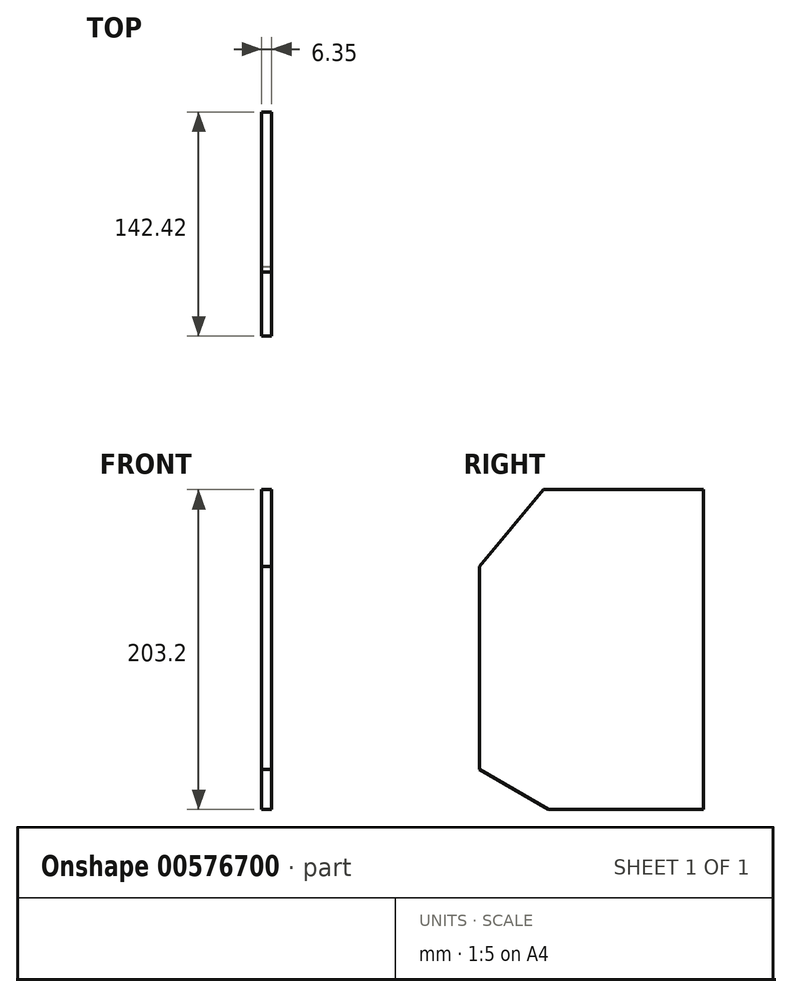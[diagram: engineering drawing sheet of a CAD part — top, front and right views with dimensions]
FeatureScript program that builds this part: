
annotation { "Feature Type Name" : "Feature", "Feature Type Description" : "" }
export const myFeature = defineFeature(function(context is Context, id is Id, definition is map)
    precondition{}
    {
        {
            var Q0;
            Q0=qCreatedBy(makeId("Right.planeOp"),FACE);
            var sketch = newSketch(context, id + "F0", { "sketchPlane" : qUnion([Q0])});
            skLineSegment(sketch, "E0.bottom", {"start": v(71.2, 101.6) * mm, "end": v(-30.4, 101.6) * mm});
            skLineSegment(sketch, "E0.top", {"start": v(71.2, -101.6) * mm, "end": v(-27.21, -101.6) * mm});
            skLineSegment(sketch, "E0.left", {"start": v(71.2, 101.6) * mm, "end": v(71.2, -101.6) * mm});
            skLineSegment(sketch, "E0.right", {"start": v(-71.2, 52.96) * mm, "end": v(-71.2, -76.2) * mm});
            skPoint(sketch, "E0.middle", {"position": v(0, 0) * mm});
            skLineSegment(sketch, "E1", {"start": v(-30.4, 101.6) * mm, "end": v(-71.2, 52.96) * mm});
            skPoint(sketch, "E2.orphan", {"position": v(-71.2, 101.6) * mm});
            skLineSegment(sketch, "E3", {"start": v(-71.2, -76.2) * mm, "end": v(-27.21, -101.6) * mm});
            skPoint(sketch, "E4.orphan", {"position": v(-71.2, -101.6) * mm});
            skSolve(sketch);
        }
        {
            var Q0;
            Q0 = qSketchRegion(id + "F0", true);
            extrude(context, id + "F1", {"entities" : qUnion([Q0]), "depth" : 6.35 * mm, "offsetDistance" : 25.4 * mm});
        }
    });
